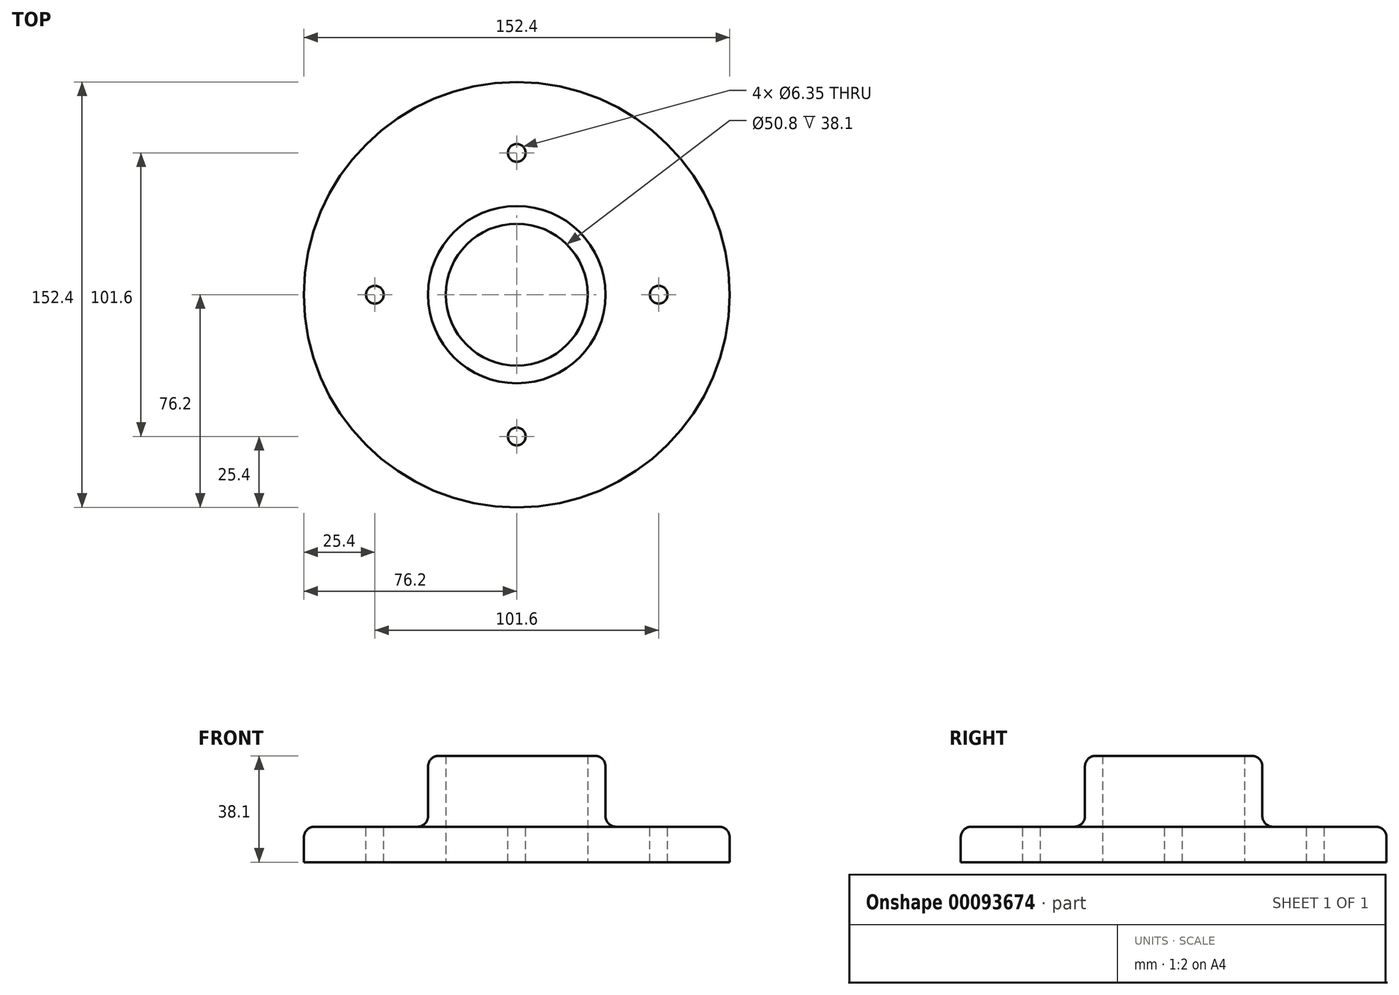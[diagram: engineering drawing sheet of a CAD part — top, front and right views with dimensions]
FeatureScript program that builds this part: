
annotation { "Feature Type Name" : "Feature", "Feature Type Description" : "" }
export const myFeature = defineFeature(function(context is Context, id is Id, definition is map)
    precondition{}
    {
        {
            var Q0;
            Q0=qCreatedBy(makeId("Top.planeOp"),FACE);
            var sketch = newSketch(context, id + "F0", { "sketchPlane" : qUnion([Q0])});
            skCircle(sketch, "E0", {"center": v(0, 0) * mm, "radius": 76.2 * mm});
            skCircle(sketch, "E1", {"center": v(0, 0) * mm, "radius": 25.4 * mm});
            skSolve(sketch);
        }
        {
            var Q0;
            Q0=makeQuery(id+"F0.imprint","IMPRINT",FACE,{"disambiguationData":[TD([[makeQuery(id+"F0.imprint","IMPRINT",EDGE,{"derivedFrom":sQuery(id+"F0.wireOp",EDGE,"E0")}),1.0]])]});
            extrude(context, id + "F1", {"entities" : qUnion([Q0]), "depth" : 12.7 * mm});
        }
        {
            var Q0;
            Q0=qCreatedBy(makeId("Top.planeOp"),FACE);
            var sketch = newSketch(context, id + "F2", { "sketchPlane" : qUnion([Q0])});
            skCircle(sketch, "E2", {"center": v(0, 0) * mm, "radius": 31.75 * mm});
            skCircle(sketch, "E3", {"center": v(0, 0) * mm, "radius": 25.4 * mm});
            skSolve(sketch);
        }
        {
            var Q0;
            Q0=makeQuery(id+"F2.imprint","IMPRINT",FACE,{"disambiguationData":[TD([[makeQuery(id+"F2.imprint","IMPRINT",EDGE,{"derivedFrom":sQuery(id+"F2.wireOp",EDGE,"E2")}),1.0]])]});
            extrude(context, id + "F3", {"entities" : qUnion([Q0]), "operationType" : NewBodyOperationType.ADD, "depth" : 38.1 * mm});
        }
        {
            var Q0;
            Q0=makeQuery(id+"F1.opExtrude","CAP_FACE",FACE,{"disambiguationData":[OSD([sQuery(id+"F0.wireOp",EDGE,"E0"),sQuery(id+"F0.wireOp",EDGE,"E1")])],"isStart":false});
            var sketch = newSketch(context, id + "F4", { "sketchPlane" : qUnion([Q0])});
            skCircle(sketch, "E4", {"center": v(-50.8, 0) * mm, "radius": 3.18 * mm});
            skCircle(sketch, "E5.1.0", {"center": v(0, -50.8) * mm, "radius": 3.18 * mm});
            skCircle(sketch, "E5.2.0", {"center": v(50.8, 0) * mm, "radius": 3.18 * mm});
            skCircle(sketch, "E5.3.0", {"center": v(0, 50.8) * mm, "radius": 3.18 * mm});
            skPoint(sketch, "E5.center", {"position": v(0, 0) * mm});
            skSolve(sketch);
        }
        {
            var Q0;
            Q0=qSketchRegion(id+"F4",true);
            extrude(context, id + "F5", {"entities" : qUnion([Q0]), "operationType" : NewBodyOperationType.REMOVE, "endBound" : BoundingType.THROUGH_ALL, "oppositeDirection" : true, "depth" : 25.4 * mm});
        }
        {
            var Q0;
            Q0=makeQuery(id+"F1.opExtrude","CAP_EDGE",EDGE,{"disambiguationData":[OSD([sQuery(id+"F0.wireOp",EDGE,"E0")])],"isStart":false});
            var Q1;
            Q1=makeQuery(id+"F3.opExtrude","CAP_EDGE",EDGE,{"disambiguationData":[OSD([sQuery(id+"F2.wireOp",EDGE,"E2")])],"isStart":false});
            var Q2;
            Q2=makeQuery(id+"F3.boolean.opBoolean","INTERSECT",EDGE,{"derivedFrom":[makeQuery(id+"F1.opExtrude","CAP_FACE",FACE,{"disambiguationData":[OSD([sQuery(id+"F0.wireOp",EDGE,"E0"),sQuery(id+"F0.wireOp",EDGE,"E1")])],"isStart":false}),makeQuery(id+"F3.opExtrude","SWEPT_FACE",FACE,{"disambiguationData":[OSD([sQuery(id+"F2.wireOp",EDGE,"E2")])]})]});
            fillet(context, id + "F6", {"entities" : qUnion([Q0, Q1, Q2]), "radius" : 3.8 * mm, "tangentPropagation" : true, "allowEdgeOverflow" : false});
        }
    });
